# Revit family: Toilet_Seat-Round-American_Standard-Telescoping_Luxury-5025B.65G
name_source: partatom
category: Specialty Equipment
revit_build: Autodesk Revit 2014 (Build: 20130308_1515(x64)
units: mm (PartAtom-declared; Revit-internal decimal feet)

## types (1)
- 5025B.65G
    Assembly Code = C1030200
    Default Elevation = 0"
    Description = American Standard Round Front Telescoping Luxury Seat With Slow Close and Everclean
    Height = 2 3/16"
    Hole Location = 5 1/2"
    Installation Type = Surface Mounted
    Length = 16 11/16"
    Manufacturer = American Standard
    Material = Plastic-American Standard-020-White
    Model = 5025B.65G
    Price = Prices may vary. Please consult Manufacturer Representative for most up-to-date price list.
    Product Documentation Link = https://www.americanstandard-us.com
    Product Page URL = https://www.americanstandard-us.com
    Shipping Weight = 3.9 lb
    URL = https://www.americanstandard-us.com
    Warranty Information = 1 Year Limited Warranty
    Width = 14 7/16"

## geometry (parser evidence)
native form markers: Sweep x1
no freeform markers — native parametric forms only
